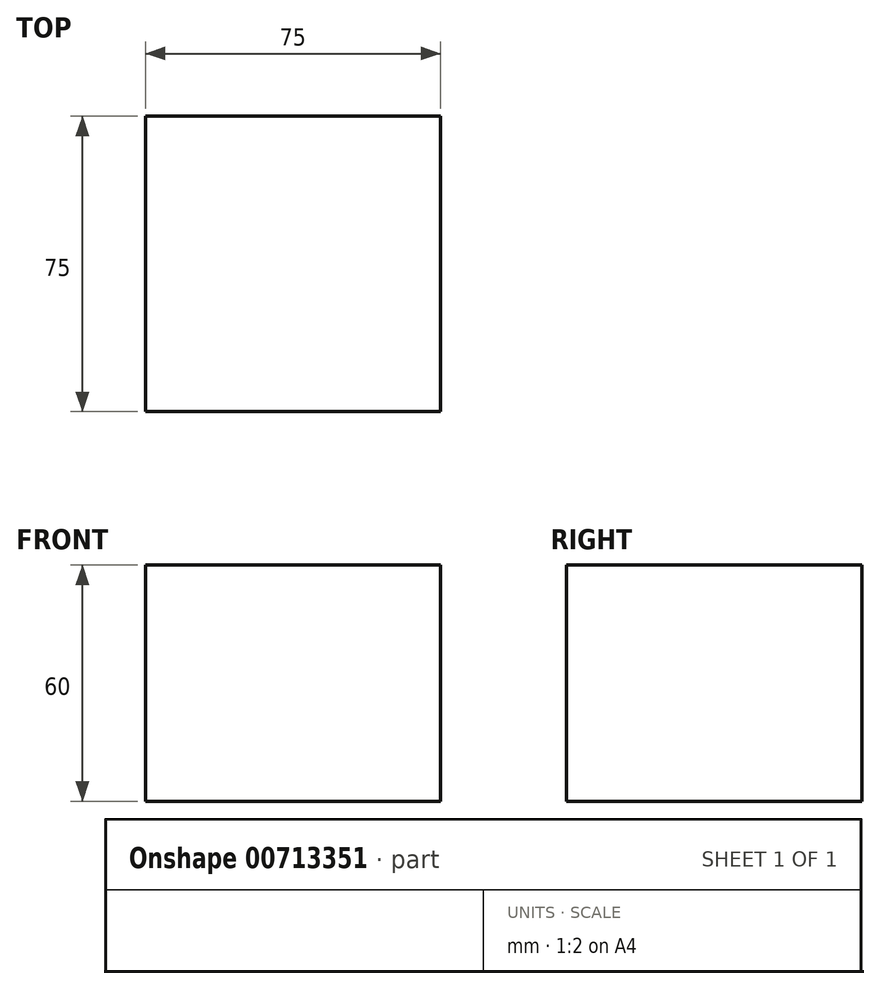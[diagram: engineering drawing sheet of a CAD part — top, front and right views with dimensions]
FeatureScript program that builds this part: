
annotation { "Feature Type Name" : "Feature", "Feature Type Description" : "" }
export const myFeature = defineFeature(function(context is Context, id is Id, definition is map)
    precondition{}
    {
        {
            var Q0;
            Q0=qCreatedBy(makeId("Front.planeOp"),FACE);
            var sketch = newSketch(context, id + "F0", { "sketchPlane" : qUnion([Q0])});
            skLineSegment(sketch, "E0.bottom", {"start": v(-25, 30) * mm, "end": v(25, 30) * mm});
            skLineSegment(sketch, "E0.top", {"start": v(-25, -30) * mm, "end": v(25, -30) * mm});
            skLineSegment(sketch, "E0.left", {"start": v(-25, 30) * mm, "end": v(-25, -30) * mm});
            skLineSegment(sketch, "E0.right", {"start": v(25, 30) * mm, "end": v(25, -30) * mm});
            skPoint(sketch, "E0.middle", {"position": v(0, 0) * mm});
            skSolve(sketch);
        }
        {
            var Q0;
            Q0 = qSketchRegion(id + "F0", true);
            extrude(context, id + "F1", {"entities" : qUnion([Q0]), "depth" : 25 * mm, "offsetDistance" : 25 * mm});
        }
        {
            var Q0;
            Q0=makeQuery(id+"F1.opExtrude","CAP_FACE",FACE,{"disambiguationData":[OSD([sQuery(id+"F0.wireOp",EDGE,"E0.bottom"),sQuery(id+"F0.wireOp",EDGE,"E0.top"),sQuery(id+"F0.wireOp",EDGE,"E0.left"),sQuery(id+"F0.wireOp",EDGE,"E0.right")])],"isStart":false});
            extrude(context, id + "F2", {"entities" : qUnion([Q0]), "operationType" : NewBodyOperationType.ADD, "depth" : 50 * mm, "offsetDistance" : 25 * mm});
        }
        {
            var Q0;
            {var subQ0=sQuery(id+"F0.wireOp",EDGE,"E0.right");Q0=makeQuery(id+"F2.boolean.opBoolean","MERGE",FACE,{"derivedFrom":[makeQuery(id+"F1.opExtrude","SWEPT_FACE",FACE,{"disambiguationData":[OSD([subQ0])]}),makeQuery(id+"F2.opExtrude","SWEPT_FACE",FACE,{"disambiguationData":[OSD([subQ0])]})]});}
            extrude(context, id + "F3", {"entities" : qUnion([Q0]), "operationType" : NewBodyOperationType.ADD, "depth" : 25 * mm, "offsetDistance" : 25 * mm});
        }
    });
